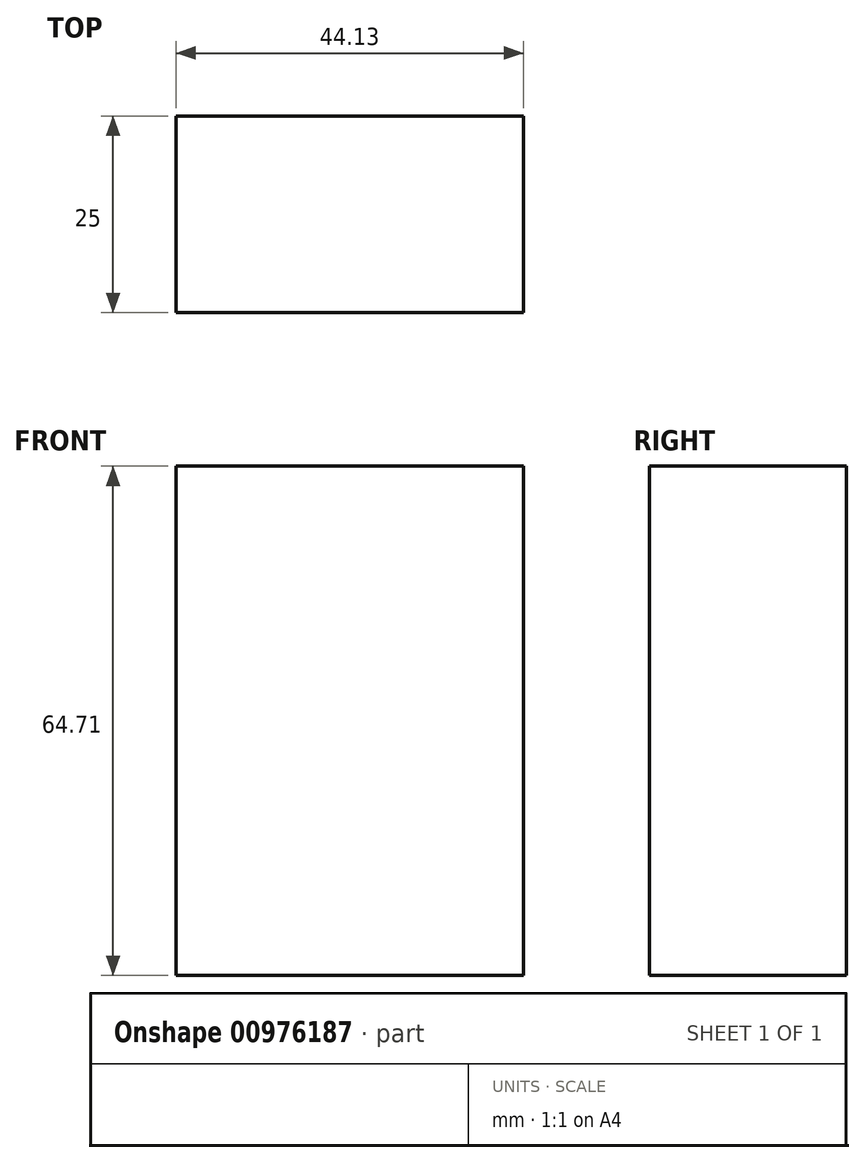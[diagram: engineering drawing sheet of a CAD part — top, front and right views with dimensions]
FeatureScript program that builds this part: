
annotation { "Feature Type Name" : "Feature", "Feature Type Description" : "" }
export const myFeature = defineFeature(function(context is Context, id is Id, definition is map)
    precondition{}
    {
        {
            var Q0;
            Q0=qCreatedBy(makeId("Front.planeOp"),FACE);
            var sketch = newSketch(context, id + "F0", { "sketchPlane" : qUnion([Q0])});
            skLineSegment(sketch, "E0.bottom", {"start": v(-121.72, 43.04) * mm, "end": v(-77.59, 43.04) * mm});
            skLineSegment(sketch, "E0.top", {"start": v(-121.72, -21.67) * mm, "end": v(-77.59, -21.67) * mm});
            skLineSegment(sketch, "E0.left", {"start": v(-121.72, 43.04) * mm, "end": v(-121.72, -21.67) * mm});
            skLineSegment(sketch, "E0.right", {"start": v(-77.59, 43.04) * mm, "end": v(-77.59, -21.67) * mm});
            skSolve(sketch);
        }
        {
            var Q0;
            Q0 = qSketchRegion(id + "F0", true);
            extrude(context, id + "F1", {"entities" : qUnion([Q0]), "depth" : 25 * mm, "offsetDistance" : 25 * mm});
        }
    });
